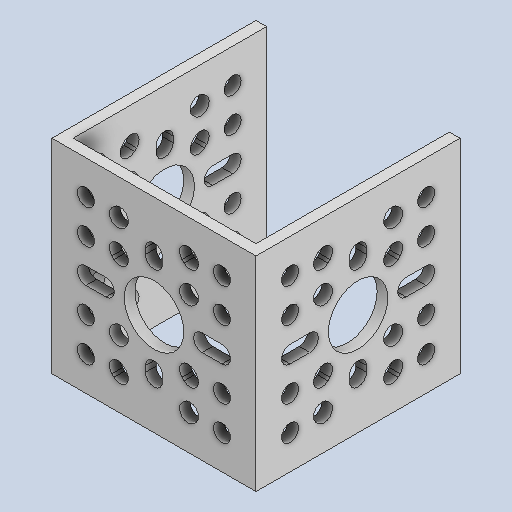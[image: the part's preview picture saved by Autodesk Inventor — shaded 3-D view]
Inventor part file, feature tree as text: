
AUTODESK INVENTOR PART (.ipt)
format: ipt  version: 2023 (Build 270158000, 158)  size: 375,296 bytes
history: native  units: in
note: dims shown in document units (in); Inventor stores cm internally (conversion verified against a paired STEP export)
features: mirror x1
ambient origin geometry x8: Origin, YZ Plane, XZ Plane, XY Plane, X Axis, Y Axis, Z Axis, Center Point
bodies: Solid1 (feature_tree)
feature tree (1):
  mirror  "Mirror6"
